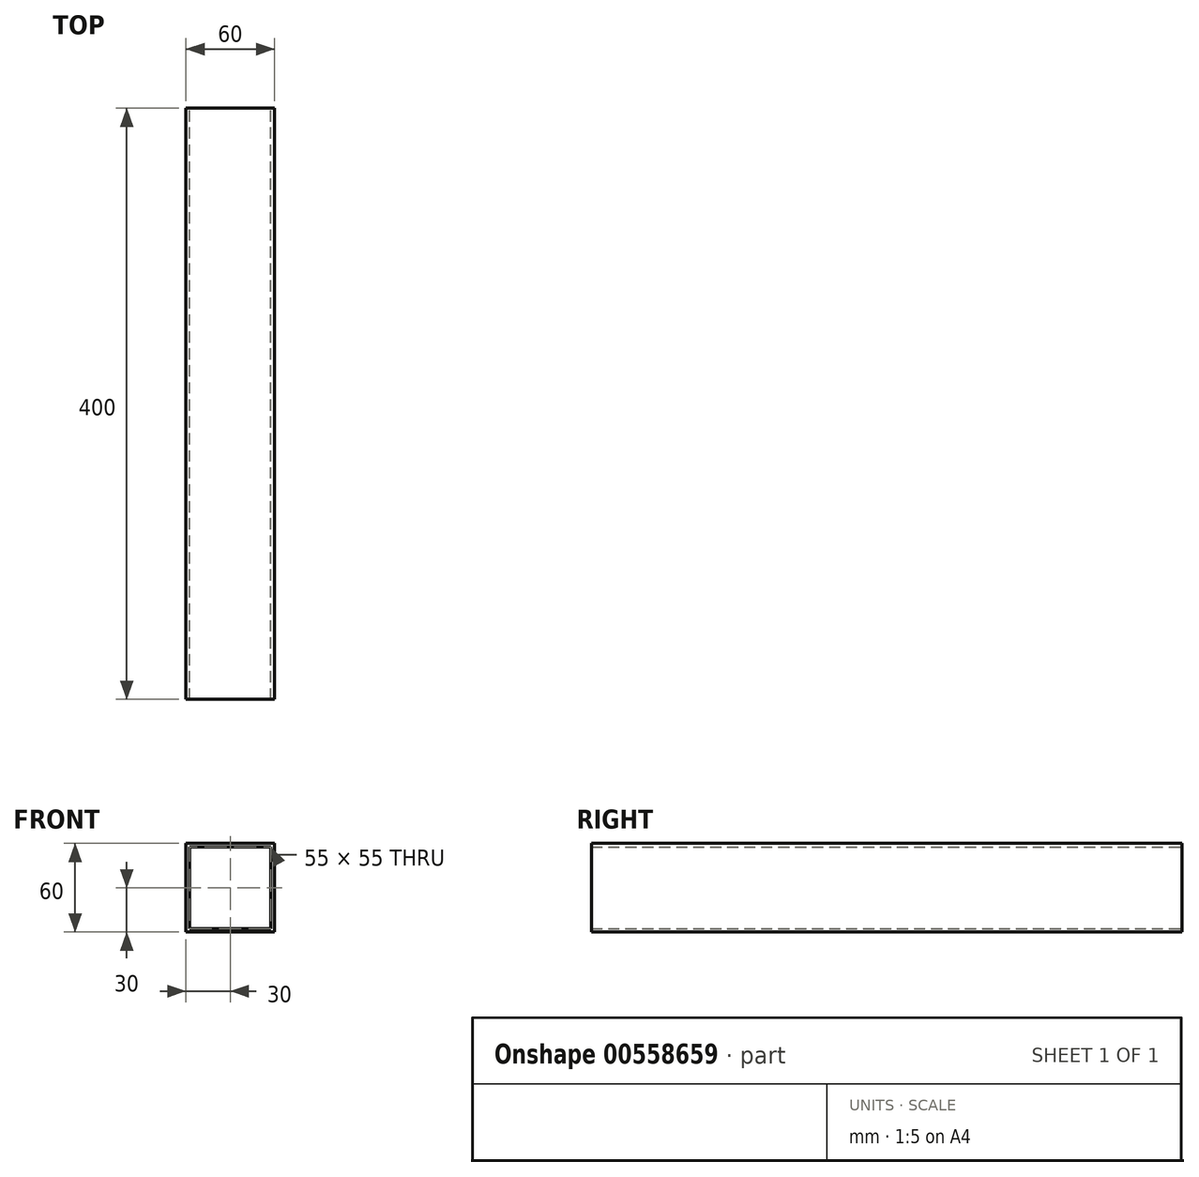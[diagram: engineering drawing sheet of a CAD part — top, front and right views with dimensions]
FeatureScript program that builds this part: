
annotation { "Feature Type Name" : "Feature", "Feature Type Description" : "" }
export const myFeature = defineFeature(function(context is Context, id is Id, definition is map)
    precondition{}
    {
        {
            var Q0;
            Q0=qCreatedBy(makeId("Front.planeOp"),FACE);
            var sketch = newSketch(context, id + "F0", { "sketchPlane" : qUnion([Q0])});
            skLineSegment(sketch, "E0.bottom", {"start": v(-30, -30) * mm, "end": v(30, -30) * mm});
            skLineSegment(sketch, "E0.top", {"start": v(-30, 30) * mm, "end": v(30, 30) * mm});
            skLineSegment(sketch, "E0.left", {"start": v(-30, -30) * mm, "end": v(-30, 30) * mm});
            skLineSegment(sketch, "E0.right", {"start": v(30, -30) * mm, "end": v(30, 30) * mm});
            skPoint(sketch, "E0.middle", {"position": v(0, 0) * mm});
            skLineSegment(sketch, "E1.bottom", {"start": v(-27.5, -27.5) * mm, "end": v(27.5, -27.5) * mm});
            skLineSegment(sketch, "E1.top", {"start": v(-27.5, 27.5) * mm, "end": v(27.5, 27.5) * mm});
            skLineSegment(sketch, "E1.left", {"start": v(-27.5, -27.5) * mm, "end": v(-27.5, 27.5) * mm});
            skLineSegment(sketch, "E1.right", {"start": v(27.5, -27.5) * mm, "end": v(27.5, 27.5) * mm});
            skSolve(sketch);
        }
        {
            var Q0;
            Q0 = qSketchRegion(id + "F0", true);
            extrude(context, id + "F1", {"entities" : qUnion([Q0]), "depth" : 400 * mm, "offsetDistance" : 25 * mm});
        }
    });
